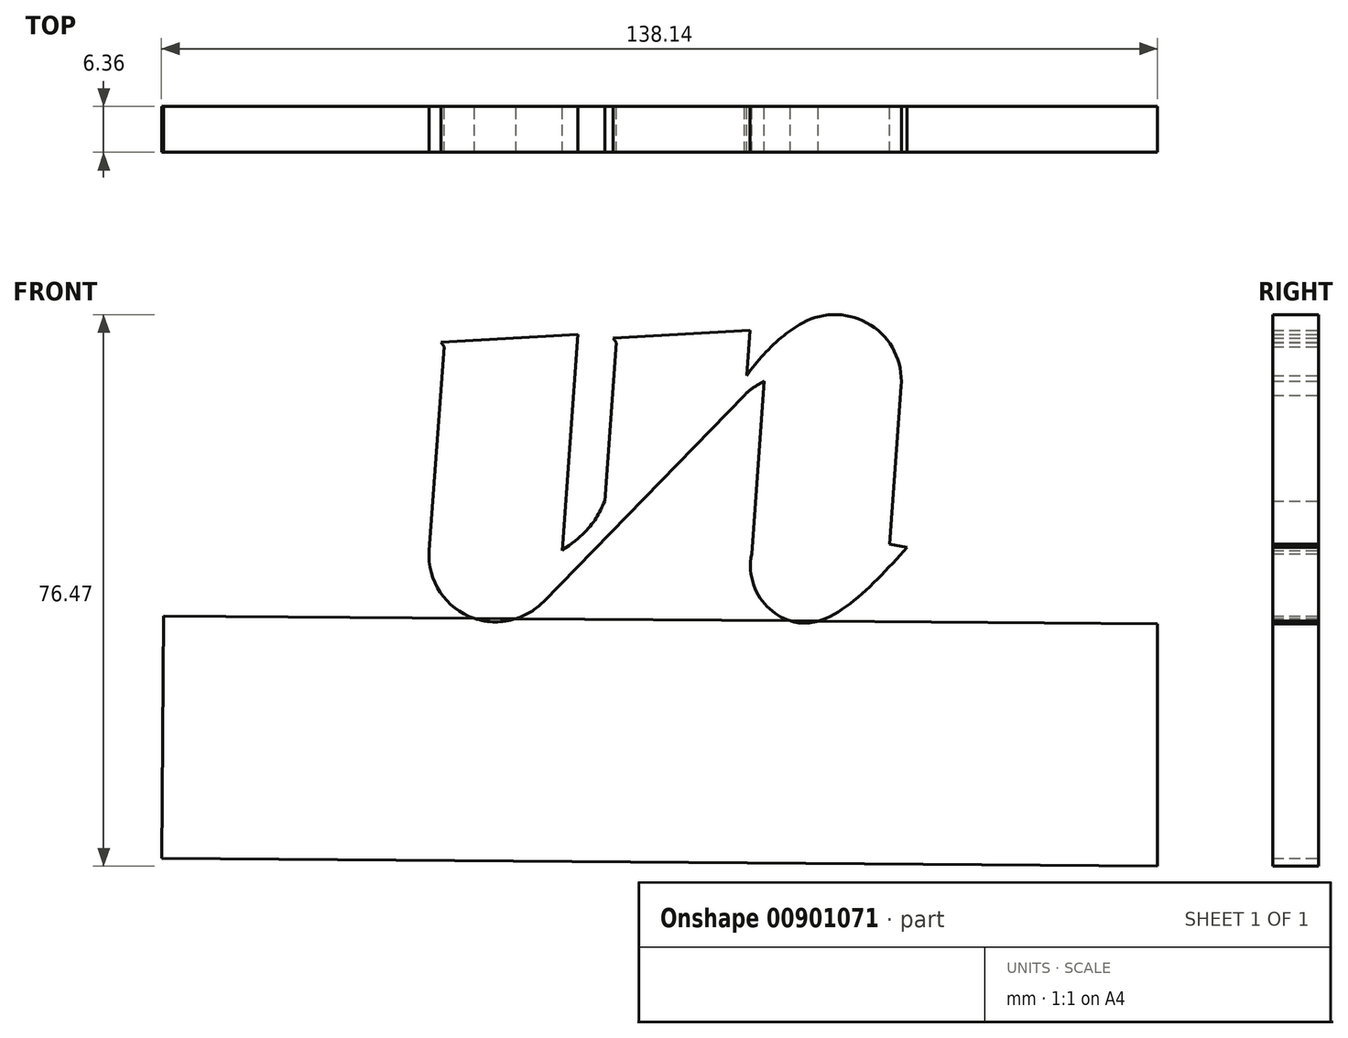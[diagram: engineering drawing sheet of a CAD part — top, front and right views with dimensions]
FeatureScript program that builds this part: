
annotation { "Feature Type Name" : "Feature", "Feature Type Description" : "" }
export const myFeature = defineFeature(function(context is Context, id is Id, definition is map)
    precondition{}
    {
        {
            var Q0;
            Q0=qCreatedBy(makeId("Front.planeOp"),FACE);
            var sketch = newSketch(context, id + "F0", { "sketchPlane" : qUnion([Q0])});
            skLineSegment(sketch, "E0", {"start": v(0, 0) * mm, "end": v(-2.18, -29.92) * mm});
            skLineSegment(sketch, "E1", {"start": v(0, 0) * mm, "end": v(-18.97, -1.04) * mm});
            skLineSegment(sketch, "E2", {"start": v(-18.97, -1.04) * mm, "end": v(-18.56, -1.7) * mm});
            skLineSegment(sketch, "E3", {"start": v(-18.56, -1.7) * mm, "end": v(-20.62, -29.92) * mm});
            skArc(sketch, "E4", {"start": v(-20.62, -29.92) * mm, "mid": v(-15.19, -39.02) * mm, "end": v(-4.78, -37.04) * mm});
            skLineSegment(sketch, "E5", {"start": v(23.88, 0.57) * mm, "end": v(4.9, -0.46) * mm});
            skLineSegment(sketch, "E6", {"start": v(4.9, -0.46) * mm, "end": v(5.32, -1.12) * mm});
            skLineSegment(sketch, "E7", {"start": v(5.32, -1.12) * mm, "end": v(3.72, -23.06) * mm});
            skFitSpline(sketch, "E8", {"points": [v(3.72, -23.06) * mm, v(-2.18, -29.92) * mm], "startDerivative": vector(-3.3, -7.53) * mm, "endDerivative": vector(-11.77, -8.1) * mm});
            skLineSegment(sketch, "E9", {"start": v(23.88, 0.57) * mm, "end": v(23.42, -5.71) * mm});
            skLineSegment(sketch, "E10", {"start": v(-4.78, -37.04) * mm, "end": v(23.1, -8.41) * mm});
            skFitSpline(sketch, "E11", {"points": [v(23.42, -5.71) * mm, v(31.2, 1.64) * mm], "startDerivative": vector(6.17, 8.88) * mm, "endDerivative": vector(8.92, 4.9) * mm});
            skFitSpline(sketch, "E12", {"points": [v(23.1, -8.41) * mm, v(25.85, -6.48) * mm], "startDerivative": vector(2.58, 2.84) * mm, "endDerivative": vector(2.36, 1.18) * mm});
            skLineSegment(sketch, "E13", {"start": v(25.85, -6.48) * mm, "end": v(24.1, -30.42) * mm});
            skLineSegment(sketch, "E14", {"start": v(44.86, -7.12) * mm, "end": v(43.26, -29.06) * mm});
            skArc(sketch, "E15", {"start": v(44.86, -7.12) * mm, "mid": v(40.63, 1.32) * mm, "end": v(31.2, 1.64) * mm});
            skLineSegment(sketch, "E16", {"start": v(43.26, -29.06) * mm, "end": v(45.67, -29.51) * mm});
            skFitSpline(sketch, "E17", {"points": [v(24.1, -30.42) * mm, v(31.13, -39.99) * mm, v(45.67, -29.51) * mm], "startDerivative": vector(-6.89, -34.38) * mm, "endDerivative": vector(24.04, 26.04) * mm});
            skLineSegment(sketch, "E18", {"start": v(80.39, -40.08) * mm, "end": v(-57.5, -39.02) * mm});
            skPoint(sketch, "E18.endSnap0", {"position": v(-15.19, -39.02) * mm});
            skLineSegment(sketch, "E19", {"start": v(-57.5, -39.02) * mm, "end": v(-57.75, -72.64) * mm});
            skLineSegment(sketch, "E20", {"start": v(-57.75, -72.64) * mm, "end": v(80.39, -73.7) * mm});
            skLineSegment(sketch, "E21", {"start": v(80.39, -73.7) * mm, "end": v(80.39, -40.08) * mm});
            skSolve(sketch);
        }
        {
            var Q0;
            Q0=makeQuery(id+"F0.imprint","IMPRINT",FACE,{"disambiguationData":[TD([[makeQuery(id+"F0.imprint","IMPRINT",EDGE,{"derivedFrom":sQuery(id+"F0.wireOp",EDGE,"E0")}),-1.0]])]});
            var Q1;
            {var subQ0=sQuery(id+"F0.wireOp",EDGE,"E18");var subQ1=sQuery(id+"F0.wireOp",EDGE,"E4");var subQ2=makeQuery(id+"F0.imprint","INTERSECT",VERTEX,{"disambiguationData":[OD(0.0)],"derivedFrom":[subQ1,subQ0]});Q1=makeQuery(id+"F0.imprint","IMPRINT",FACE,{"disambiguationData":[TD([[makeQuery(id+"F0.imprint","IMPRINT",EDGE,{"disambiguationData":[TD([[subQ2,-1.0]])],"derivedFrom":subQ1}),1.0]])]});}
            var Q2;
            {var subQ0=sQuery(id+"F0.wireOp",EDGE,"E18");var subQ1=sQuery(id+"F0.wireOp",EDGE,"E17");var subQ2=makeQuery(id+"F0.imprint","INTERSECT",VERTEX,{"disambiguationData":[OD(0.0)],"derivedFrom":[subQ1,subQ0]});Q2=makeQuery(id+"F0.imprint","IMPRINT",FACE,{"disambiguationData":[TD([[makeQuery(id+"F0.imprint","IMPRINT",EDGE,{"disambiguationData":[TD([[subQ2,1.0]])],"derivedFrom":subQ1}),1.0]])]});}
            var Q3;
            {var subQ8=sQuery(id+"F0.wireOp",EDGE,"E19");Q3=makeQuery(id+"F0.imprint","IMPRINT",FACE,{"disambiguationData":[TD([[makeQuery(id+"F0.imprint","IMPRINT",EDGE,{"derivedFrom":subQ8}),1.0]])]});}
            extrude(context, id + "F1", {"entities" : qUnion([Q0, Q1, Q2, Q3]), "endBound" : BoundingType.SYMMETRIC, "depth" : 6.35 * mm, "offsetDistance" : 25.4 * mm});
        }
    });
